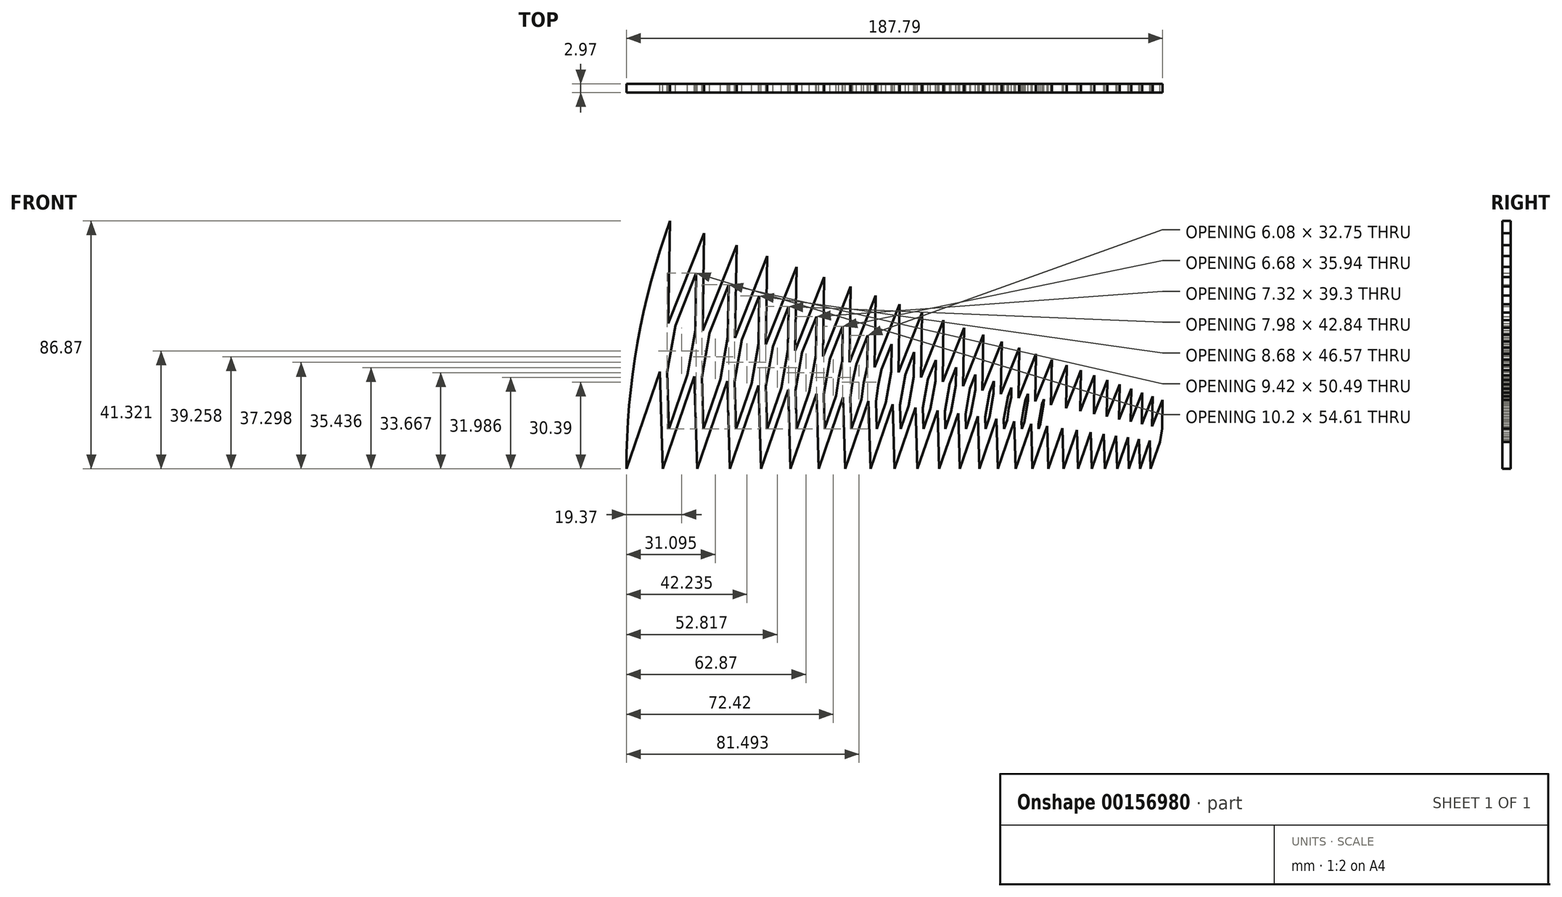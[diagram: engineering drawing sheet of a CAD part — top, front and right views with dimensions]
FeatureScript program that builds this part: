
annotation { "Feature Type Name" : "Feature", "Feature Type Description" : "" }
export const myFeature = defineFeature(function(context is Context, id is Id, definition is map)
    precondition{}
    {
        {
            var Q0;
            Q0=qCreatedBy(makeId("Front.planeOp"),FACE);
            var sketch = newSketch(context, id + "F0", { "sketchPlane" : qUnion([Q0])});
            skLineSegment(sketch, "E0", {"start": v(-94.98, 0) * mm, "end": v(159.02, 0) * mm, "construction": true});
            skLineSegment(sketch, "E1", {"start": v(159.02, 0) * mm, "end": v(-91.12, 44.1) * mm, "construction": true});
            skLineSegment(sketch, "E2", {"start": v(159.02, 0) * mm, "end": v(-92.51, 35.35) * mm, "construction": true});
            skLineSegment(sketch, "E3", {"start": v(91.81, 9.44) * mm, "end": v(88.56, 0) * mm});
            skLineSegment(sketch, "E4", {"start": v(88.56, 0) * mm, "end": v(88.28, 9.94) * mm});
            skLineSegment(sketch, "E5", {"start": v(88.28, 9.94) * mm, "end": v(84.85, 0) * mm});
            skLineSegment(sketch, "E6", {"start": v(84.85, 0) * mm, "end": v(84.55, 10.47) * mm});
            skLineSegment(sketch, "E7", {"start": v(84.55, 10.47) * mm, "end": v(80.95, 0) * mm});
            skLineSegment(sketch, "E8", {"start": v(80.95, 0) * mm, "end": v(80.63, 11.02) * mm});
            skLineSegment(sketch, "E9", {"start": v(80.63, 11.02) * mm, "end": v(76.84, 0) * mm});
            skLineSegment(sketch, "E10", {"start": v(76.84, 0) * mm, "end": v(76.5, 11.6) * mm});
            skLineSegment(sketch, "E11", {"start": v(76.5, 11.6) * mm, "end": v(72.51, 0) * mm});
            skLineSegment(sketch, "E12", {"start": v(72.51, 0) * mm, "end": v(72.17, 12.2) * mm});
            skLineSegment(sketch, "E13", {"start": v(72.17, 12.2) * mm, "end": v(67.96, 0) * mm});
            skLineSegment(sketch, "E14", {"start": v(67.96, 0) * mm, "end": v(67.6, 12.85) * mm});
            skLineSegment(sketch, "E15", {"start": v(67.6, 12.85) * mm, "end": v(63.17, 0) * mm});
            skLineSegment(sketch, "E16", {"start": v(63.17, 0) * mm, "end": v(62.78, 13.52) * mm});
            skLineSegment(sketch, "E17", {"start": v(62.78, 13.52) * mm, "end": v(58.12, 0) * mm});
            skLineSegment(sketch, "E18", {"start": v(58.12, 0) * mm, "end": v(57.72, 14.24) * mm});
            skLineSegment(sketch, "E19", {"start": v(57.72, 14.24) * mm, "end": v(52.81, 0) * mm});
            skLineSegment(sketch, "E20", {"start": v(52.81, 0) * mm, "end": v(52.39, 14.99) * mm});
            skLineSegment(sketch, "E21", {"start": v(52.39, 14.99) * mm, "end": v(47.22, 0) * mm});
            skLineSegment(sketch, "E22", {"start": v(47.22, 0) * mm, "end": v(46.77, 15.77) * mm});
            skLineSegment(sketch, "E23", {"start": v(46.77, 15.77) * mm, "end": v(41.34, 0) * mm});
            skLineSegment(sketch, "E24", {"start": v(41.34, 0) * mm, "end": v(40.87, 16.6) * mm});
            skLineSegment(sketch, "E25", {"start": v(40.87, 16.6) * mm, "end": v(35.15, 0) * mm});
            skLineSegment(sketch, "E26", {"start": v(35.15, 0) * mm, "end": v(34.65, 17.48) * mm});
            skLineSegment(sketch, "E27", {"start": v(34.65, 17.48) * mm, "end": v(28.63, 0) * mm});
            skLineSegment(sketch, "E28", {"start": v(28.63, 0) * mm, "end": v(28.1, 18.4) * mm});
            skLineSegment(sketch, "E29", {"start": v(28.1, 18.4) * mm, "end": v(21.77, 0) * mm});
            skLineSegment(sketch, "E30", {"start": v(21.77, 0) * mm, "end": v(21.21, 19.37) * mm});
            skLineSegment(sketch, "E31", {"start": v(21.21, 19.37) * mm, "end": v(14.54, 0) * mm});
            skLineSegment(sketch, "E32", {"start": v(14.54, 0) * mm, "end": v(13.96, 20.39) * mm});
            skLineSegment(sketch, "E33", {"start": v(13.96, 20.39) * mm, "end": v(6.94, 0) * mm});
            skLineSegment(sketch, "E34", {"start": v(6.94, 0) * mm, "end": v(6.33, 21.46) * mm});
            skLineSegment(sketch, "E35", {"start": v(6.33, 21.46) * mm, "end": v(-1.07, 0) * mm});
            skLineSegment(sketch, "E36", {"start": v(-1.07, 0) * mm, "end": v(-1.71, 22.59) * mm});
            skLineSegment(sketch, "E37", {"start": v(-1.71, 22.59) * mm, "end": v(-9.5, 0) * mm});
            skLineSegment(sketch, "E38", {"start": v(-18.36, 0) * mm, "end": v(-19.07, 25.03) * mm});
            skLineSegment(sketch, "E39", {"start": v(-19.07, 25.03) * mm, "end": v(-27.7, 0) * mm});
            skLineSegment(sketch, "E40", {"start": v(-27.7, 0) * mm, "end": v(-28.45, 26.35) * mm});
            skLineSegment(sketch, "E41", {"start": v(-28.45, 26.35) * mm, "end": v(-37.52, 0) * mm});
            skLineSegment(sketch, "E42", {"start": v(-37.52, 0) * mm, "end": v(-38.31, 27.73) * mm});
            skLineSegment(sketch, "E43", {"start": v(-38.31, 27.73) * mm, "end": v(-47.87, 0) * mm});
            skLineSegment(sketch, "E44", {"start": v(-47.87, 0) * mm, "end": v(-48.7, 29.2) * mm});
            skLineSegment(sketch, "E45", {"start": v(-48.7, 29.2) * mm, "end": v(-58.76, 0) * mm});
            skLineSegment(sketch, "E46", {"start": v(-18.36, 0) * mm, "end": v(-10.17, 23.78) * mm});
            skLineSegment(sketch, "E47", {"start": v(-10.17, 23.78) * mm, "end": v(-9.5, 0) * mm});
            skLineSegment(sketch, "E48", {"start": v(-58.76, 0) * mm, "end": v(-59.63, 30.73) * mm});
            skLineSegment(sketch, "E49", {"start": v(-59.63, 30.73) * mm, "end": v(-70.22, 0) * mm});
            skLineSegment(sketch, "E50", {"start": v(-70.22, 0) * mm, "end": v(-71.14, 32.35) * mm});
            skLineSegment(sketch, "E51", {"start": v(-71.14, 32.35) * mm, "end": v(-82.28, 0) * mm});
            skLineSegment(sketch, "E52", {"start": v(-82.28, 0) * mm, "end": v(-83.25, 34.05) * mm});
            skLineSegment(sketch, "E53", {"start": v(-83.25, 34.05) * mm, "end": v(-94.98, 0) * mm});
            skLineSegment(sketch, "E54.MirrorCS", {"start": v(-80.29, 50.87) * mm, "end": v(-79.67, 86.87) * mm});
            skLineSegment(sketch, "E55.MirrorCS", {"start": v(-67.73, 82.53) * mm, "end": v(-80.29, 50.87) * mm});
            skLineSegment(sketch, "E56.MirrorCS", {"start": v(-56.4, 78.4) * mm, "end": v(-68.32, 48.32) * mm});
            skLineSegment(sketch, "E57.MirrorCS", {"start": v(-56.96, 45.9) * mm, "end": v(-56.4, 78.4) * mm});
            skLineSegment(sketch, "E58.MirrorCS", {"start": v(-45.62, 74.48) * mm, "end": v(-56.96, 45.9) * mm});
            skLineSegment(sketch, "E59.MirrorCS", {"start": v(-46.16, 43.61) * mm, "end": v(-45.62, 74.48) * mm});
            skLineSegment(sketch, "E60.MirrorCS", {"start": v(-35.4, 70.76) * mm, "end": v(-46.16, 43.61) * mm});
            skLineSegment(sketch, "E61.MirrorCS", {"start": v(-35.9, 41.43) * mm, "end": v(-35.4, 70.76) * mm});
            skLineSegment(sketch, "E62.MirrorCS", {"start": v(-25.67, 67.22) * mm, "end": v(-35.9, 41.43) * mm});
            skLineSegment(sketch, "E63.MirrorCS", {"start": v(-26.15, 39.36) * mm, "end": v(-25.67, 67.22) * mm});
            skLineSegment(sketch, "E64.MirrorCS", {"start": v(-16.44, 63.86) * mm, "end": v(-26.15, 39.36) * mm});
            skLineSegment(sketch, "E65.MirrorCS", {"start": v(-16.9, 37.4) * mm, "end": v(-16.44, 63.86) * mm});
            skLineSegment(sketch, "E66.MirrorCS", {"start": v(-7.66, 60.67) * mm, "end": v(-16.9, 37.4) * mm});
            skLineSegment(sketch, "E67.MirrorCS", {"start": v(-7.66, 60.67) * mm, "end": v(-8.1, 35.52) * mm});
            skLineSegment(sketch, "E68.MirrorCS", {"start": v(-8.1, 35.52) * mm, "end": v(0.67, 57.63) * mm});
            skLineSegment(sketch, "E69.MirrorCS", {"start": v(0.26, 33.75) * mm, "end": v(0.67, 57.63) * mm});
            skLineSegment(sketch, "E70.MirrorCS", {"start": v(8.59, 54.75) * mm, "end": v(0.26, 33.75) * mm});
            skLineSegment(sketch, "E71.MirrorCS", {"start": v(8.2, 32.06) * mm, "end": v(8.59, 54.75) * mm});
            skLineSegment(sketch, "E72.MirrorCS", {"start": v(16.1, 52.01) * mm, "end": v(8.2, 32.06) * mm});
            skLineSegment(sketch, "E73.MirrorCS", {"start": v(23.25, 49.41) * mm, "end": v(15.74, 30.46) * mm});
            skLineSegment(sketch, "E74.MirrorCS", {"start": v(22.9, 28.93) * mm, "end": v(23.25, 49.41) * mm});
            skLineSegment(sketch, "E75.MirrorCS", {"start": v(30.04, 46.94) * mm, "end": v(22.9, 28.93) * mm});
            skLineSegment(sketch, "E76.MirrorCS", {"start": v(15.74, 30.46) * mm, "end": v(16.1, 52.01) * mm});
            skLineSegment(sketch, "E77.MirrorCS", {"start": v(29.7, 27.49) * mm, "end": v(30.04, 46.94) * mm});
            skLineSegment(sketch, "E78.MirrorCS", {"start": v(36.5, 44.6) * mm, "end": v(29.7, 27.49) * mm});
            skLineSegment(sketch, "E79.MirrorCS", {"start": v(36.17, 26.11) * mm, "end": v(36.5, 44.6) * mm});
            skLineSegment(sketch, "E80.MirrorCS", {"start": v(42.62, 42.37) * mm, "end": v(36.17, 26.11) * mm});
            skLineSegment(sketch, "E81.MirrorCS", {"start": v(42.31, 24.8) * mm, "end": v(42.62, 42.37) * mm});
            skLineSegment(sketch, "E82.MirrorCS", {"start": v(48.44, 40.25) * mm, "end": v(42.31, 24.8) * mm});
            skLineSegment(sketch, "E83.MirrorCS", {"start": v(48.15, 23.57) * mm, "end": v(48.44, 40.25) * mm});
            skLineSegment(sketch, "E84.MirrorCS", {"start": v(53.97, 38.24) * mm, "end": v(48.15, 23.57) * mm});
            skLineSegment(sketch, "E85.MirrorCS", {"start": v(53.7, 22.39) * mm, "end": v(53.97, 38.24) * mm});
            skLineSegment(sketch, "E86.MirrorCS", {"start": v(59.22, 36.32) * mm, "end": v(53.7, 22.39) * mm});
            skLineSegment(sketch, "E87.MirrorCS", {"start": v(58.96, 21.27) * mm, "end": v(59.22, 36.32) * mm});
            skLineSegment(sketch, "E88.MirrorCS", {"start": v(64.2, 34.5) * mm, "end": v(58.96, 21.27) * mm});
            skLineSegment(sketch, "E89.MirrorCS", {"start": v(63.96, 20.2) * mm, "end": v(64.2, 34.5) * mm});
            skLineSegment(sketch, "E90.MirrorCS", {"start": v(68.95, 32.78) * mm, "end": v(63.96, 20.2) * mm});
            skLineSegment(sketch, "E91.MirrorCS", {"start": v(68.71, 19.2) * mm, "end": v(68.95, 32.78) * mm});
            skLineSegment(sketch, "E92.MirrorCS", {"start": v(73.45, 31.14) * mm, "end": v(68.71, 19.2) * mm});
            skLineSegment(sketch, "E93.MirrorCS", {"start": v(73.23, 18.23) * mm, "end": v(73.45, 31.14) * mm});
            skLineSegment(sketch, "E94.MirrorCS", {"start": v(77.73, 29.59) * mm, "end": v(73.23, 18.23) * mm});
            skLineSegment(sketch, "E95.MirrorCS", {"start": v(77.52, 17.32) * mm, "end": v(77.73, 29.59) * mm});
            skLineSegment(sketch, "E96.MirrorCS", {"start": v(81.8, 28.1) * mm, "end": v(77.52, 17.32) * mm});
            skLineSegment(sketch, "E97.MirrorCS", {"start": v(81.6, 16.46) * mm, "end": v(81.8, 28.1) * mm});
            skLineSegment(sketch, "E98.MirrorCS", {"start": v(85.66, 26.7) * mm, "end": v(81.6, 16.46) * mm});
            skLineSegment(sketch, "E99.MirrorCS", {"start": v(85.46, 15.63) * mm, "end": v(85.66, 26.7) * mm});
            skLineSegment(sketch, "E100.MirrorCS", {"start": v(89.32, 25.37) * mm, "end": v(85.46, 15.63) * mm});
            skLineSegment(sketch, "E101.MirrorCS", {"start": v(89.14, 14.85) * mm, "end": v(89.32, 25.37) * mm});
            skLineSegment(sketch, "E102.MirrorCS", {"start": v(92.8, 24.1) * mm, "end": v(89.14, 14.85) * mm});
            skLineSegment(sketch, "E103.MirrorCS", {"start": v(92.64, 14.1) * mm, "end": v(92.8, 24.1) * mm});
            skLineSegment(sketch, "E104.MirrorCS", {"start": v(-68.32, 48.32) * mm, "end": v(-67.73, 82.53) * mm});
            skLineSegment(sketch, "E105", {"start": v(159.02, 0) * mm, "end": v(-79.67, 86.87) * mm, "construction": true});
            skArc(sketch, "E106", {"start": v(-79.67, 86.87) * mm, "mid": v(-91.12, 44.1) * mm, "end": v(-94.98, 0) * mm});
            skLineSegment(sketch, "E107", {"start": v(-83.25, 34.05) * mm, "end": v(-81.77, 42.46) * mm});
            skLineSegment(sketch, "E108", {"start": v(-71.14, 32.35) * mm, "end": v(-69.73, 40.33) * mm});
            skLineSegment(sketch, "E109", {"start": v(-59.63, 30.73) * mm, "end": v(-58.3, 38.32) * mm});
            skLineSegment(sketch, "E110", {"start": v(-48.7, 29.2) * mm, "end": v(-47.43, 36.4) * mm});
            skLineSegment(sketch, "E111", {"start": v(-38.31, 27.73) * mm, "end": v(-37.1, 34.58) * mm});
            skLineSegment(sketch, "E112.MirrorCS", {"start": v(-80.29, 50.87) * mm, "end": v(-81.77, 42.46) * mm});
            skLineSegment(sketch, "E113.MirrorCS", {"start": v(-68.32, 48.32) * mm, "end": v(-69.73, 40.33) * mm});
            skLineSegment(sketch, "E114.MirrorCS", {"start": v(-56.96, 45.9) * mm, "end": v(-58.3, 38.32) * mm});
            skLineSegment(sketch, "E115.MirrorCS", {"start": v(-46.16, 43.61) * mm, "end": v(-47.43, 36.4) * mm});
            skLineSegment(sketch, "E116.MirrorCS", {"start": v(-35.9, 41.43) * mm, "end": v(-37.1, 34.58) * mm});
            skLineSegment(sketch, "E117.0", {"start": v(-70.86, 48.57) * mm, "end": v(-70.51, 68.63) * mm});
            skLineSegment(sketch, "E117.1", {"start": v(-70.86, 48.57) * mm, "end": v(-72.23, 40.78) * mm});
            skLineSegment(sketch, "E117.2", {"start": v(-70.51, 68.63) * mm, "end": v(-77.83, 50.17) * mm});
            skLineSegment(sketch, "E117.3", {"start": v(-73.6, 32.98) * mm, "end": v(-72.23, 40.78) * mm});
            skLineSegment(sketch, "E117.4", {"start": v(-77.83, 50.17) * mm, "end": v(-79.27, 42.02) * mm});
            skLineSegment(sketch, "E117.5", {"start": v(-80.7, 33.86) * mm, "end": v(-79.27, 42.02) * mm});
            skLineSegment(sketch, "E117.6", {"start": v(-80.14, 14.02) * mm, "end": v(-80.7, 33.86) * mm});
            skLineSegment(sketch, "E117.7", {"start": v(-73.6, 32.98) * mm, "end": v(-80.14, 14.02) * mm});
            skLineSegment(sketch, "E118", {"start": v(-28.45, 26.35) * mm, "end": v(-27.3, 32.85) * mm});
            skLineSegment(sketch, "E119", {"start": v(-19.07, 25.03) * mm, "end": v(-18.2, 31.25) * mm});
            skLineSegment(sketch, "E120", {"start": v(-10.17, 23.78) * mm, "end": v(-9.34, 29.69) * mm});
            skLineSegment(sketch, "E121", {"start": v(92.64, 14.1) * mm, "end": v(91.81, 9.44) * mm});
            skLineSegment(sketch, "E122.0", {"start": v(-59.18, 64.5) * mm, "end": v(-65.87, 47.63) * mm});
            skLineSegment(sketch, "E122.1", {"start": v(-59.5, 46.15) * mm, "end": v(-59.18, 64.5) * mm});
            skLineSegment(sketch, "E122.2", {"start": v(-65.87, 47.63) * mm, "end": v(-67.23, 39.9) * mm});
            skLineSegment(sketch, "E122.3", {"start": v(-59.5, 46.15) * mm, "end": v(-60.8, 38.76) * mm});
            skLineSegment(sketch, "E122.4", {"start": v(-68.6, 32.16) * mm, "end": v(-67.23, 39.9) * mm});
            skLineSegment(sketch, "E122.5", {"start": v(-68.08, 14.02) * mm, "end": v(-68.6, 32.16) * mm});
            skLineSegment(sketch, "E122.6", {"start": v(-62.1, 31.37) * mm, "end": v(-68.08, 14.02) * mm});
            skLineSegment(sketch, "E122.7", {"start": v(-62.1, 31.37) * mm, "end": v(-60.8, 38.76) * mm});
            skLineSegment(sketch, "E123.MirrorCS", {"start": v(-26.15, 39.36) * mm, "end": v(-27.3, 32.85) * mm});
            skLineSegment(sketch, "E124.MirrorCS", {"start": v(-16.9, 37.4) * mm, "end": v(-18.2, 31.25) * mm});
            skLineSegment(sketch, "E125.MirrorCS", {"start": v(-8.1, 35.52) * mm, "end": v(-9.34, 29.69) * mm});
            skLineSegment(sketch, "E126.0", {"start": v(-48.4, 60.58) * mm, "end": v(-54.5, 45.21) * mm});
            skLineSegment(sketch, "E126.1", {"start": v(-48.7, 43.86) * mm, "end": v(-48.4, 60.58) * mm});
            skLineSegment(sketch, "E126.2", {"start": v(-54.5, 45.21) * mm, "end": v(-55.8, 37.88) * mm});
            skLineSegment(sketch, "E126.3", {"start": v(-48.7, 43.86) * mm, "end": v(-49.93, 36.84) * mm});
            skLineSegment(sketch, "E126.4", {"start": v(-57.09, 30.54) * mm, "end": v(-55.8, 37.88) * mm});
            skLineSegment(sketch, "E126.5", {"start": v(-56.62, 14.02) * mm, "end": v(-57.09, 30.54) * mm});
            skLineSegment(sketch, "E126.6", {"start": v(-51.17, 29.83) * mm, "end": v(-56.62, 14.02) * mm});
            skLineSegment(sketch, "E126.7", {"start": v(-51.17, 29.83) * mm, "end": v(-49.93, 36.84) * mm});
            skLineSegment(sketch, "E127.0", {"start": v(-38.17, 56.86) * mm, "end": v(-43.7, 42.92) * mm});
            skLineSegment(sketch, "E127.1", {"start": v(-38.44, 41.67) * mm, "end": v(-38.17, 56.86) * mm});
            skLineSegment(sketch, "E127.2", {"start": v(-43.7, 42.92) * mm, "end": v(-44.93, 35.96) * mm});
            skLineSegment(sketch, "E127.3", {"start": v(-38.44, 41.67) * mm, "end": v(-39.6, 35.02) * mm});
            skLineSegment(sketch, "E127.4", {"start": v(-46.15, 29) * mm, "end": v(-44.93, 35.96) * mm});
            skLineSegment(sketch, "E127.5", {"start": v(-45.73, 14.02) * mm, "end": v(-46.15, 29) * mm});
            skLineSegment(sketch, "E127.6", {"start": v(-40.78, 28.37) * mm, "end": v(-45.73, 14.02) * mm});
            skLineSegment(sketch, "E127.7", {"start": v(-40.78, 28.37) * mm, "end": v(-39.6, 35.02) * mm});
            skLineSegment(sketch, "E128.0", {"start": v(-28.45, 53.32) * mm, "end": v(-33.44, 40.73) * mm});
            skLineSegment(sketch, "E128.1", {"start": v(-28.69, 39.6) * mm, "end": v(-28.45, 53.32) * mm});
            skLineSegment(sketch, "E128.2", {"start": v(-33.44, 40.73) * mm, "end": v(-34.6, 34.14) * mm});
            skLineSegment(sketch, "E128.3", {"start": v(-28.69, 39.6) * mm, "end": v(-29.8, 33.3) * mm});
            skLineSegment(sketch, "E128.4", {"start": v(-35.77, 27.55) * mm, "end": v(-34.6, 34.14) * mm});
            skLineSegment(sketch, "E128.5", {"start": v(-35.38, 14.02) * mm, "end": v(-35.77, 27.55) * mm});
            skLineSegment(sketch, "E128.6", {"start": v(-30.91, 26.98) * mm, "end": v(-35.38, 14.02) * mm});
            skLineSegment(sketch, "E128.7", {"start": v(-30.91, 26.98) * mm, "end": v(-29.8, 33.3) * mm});
            skLineSegment(sketch, "E129.0", {"start": v(-19.22, 49.96) * mm, "end": v(-23.7, 38.66) * mm});
            skLineSegment(sketch, "E129.1", {"start": v(-19.43, 37.68) * mm, "end": v(-19.22, 49.96) * mm});
            skLineSegment(sketch, "E129.2", {"start": v(-23.7, 38.66) * mm, "end": v(-24.8, 32.41) * mm});
            skLineSegment(sketch, "E129.3", {"start": v(-19.43, 37.68) * mm, "end": v(-20.7, 31.69) * mm});
            skLineSegment(sketch, "E129.4", {"start": v(-25.9, 26.16) * mm, "end": v(-24.8, 32.41) * mm});
            skLineSegment(sketch, "E129.5", {"start": v(-25.56, 14.02) * mm, "end": v(-25.9, 26.16) * mm});
            skLineSegment(sketch, "E129.6", {"start": v(-21.56, 25.62) * mm, "end": v(-25.56, 14.02) * mm});
            skLineSegment(sketch, "E129.7", {"start": v(-21.56, 25.62) * mm, "end": v(-20.7, 31.69) * mm});
            skLineSegment(sketch, "E130.0", {"start": v(-10.45, 46.76) * mm, "end": v(-14.45, 36.65) * mm});
            skLineSegment(sketch, "E130.1", {"start": v(-10.45, 46.76) * mm, "end": v(-10.63, 35.81) * mm});
            skLineSegment(sketch, "E130.2", {"start": v(-14.45, 36.65) * mm, "end": v(-15.7, 30.8) * mm});
            skLineSegment(sketch, "E130.3", {"start": v(-10.63, 35.81) * mm, "end": v(-11.84, 30.13) * mm});
            skLineSegment(sketch, "E130.4", {"start": v(-16.53, 24.89) * mm, "end": v(-15.7, 30.8) * mm});
            skLineSegment(sketch, "E130.5", {"start": v(-16.22, 14.02) * mm, "end": v(-16.53, 24.89) * mm});
            skLineSegment(sketch, "E130.6", {"start": v(-16.22, 14.02) * mm, "end": v(-12.65, 24.37) * mm});
            skLineSegment(sketch, "E130.7", {"start": v(-12.65, 24.37) * mm, "end": v(-11.84, 30.13) * mm});
            skLineSegment(sketch, "E131", {"start": v(-1.71, 22.59) * mm, "end": v(-0.73, 28.17) * mm});
            skLineSegment(sketch, "E132", {"start": v(6.33, 21.46) * mm, "end": v(7.26, 26.76) * mm});
            skLineSegment(sketch, "E133", {"start": v(13.96, 20.39) * mm, "end": v(14.85, 25.42) * mm});
            skLineSegment(sketch, "E134", {"start": v(21.21, 19.37) * mm, "end": v(22.06, 24.15) * mm});
            skLineSegment(sketch, "E135.MirrorCS", {"start": v(0.26, 33.75) * mm, "end": v(-0.73, 28.17) * mm});
            skLineSegment(sketch, "E136.MirrorCS", {"start": v(8.2, 32.06) * mm, "end": v(7.26, 26.76) * mm});
            skLineSegment(sketch, "E137.MirrorCS", {"start": v(15.74, 30.46) * mm, "end": v(14.85, 25.42) * mm});
            skLineSegment(sketch, "E138.MirrorCS", {"start": v(22.9, 28.93) * mm, "end": v(22.06, 24.15) * mm});
            skLineSegment(sketch, "E139.0", {"start": v(-5.66, 34.78) * mm, "end": v(-2.11, 43.73) * mm});
            skLineSegment(sketch, "E139.1", {"start": v(-2.28, 33.99) * mm, "end": v(-2.11, 43.73) * mm});
            skLineSegment(sketch, "E139.2", {"start": v(-5.66, 34.78) * mm, "end": v(-6.84, 29.24) * mm});
            skLineSegment(sketch, "E139.3", {"start": v(-2.28, 33.99) * mm, "end": v(-3.23, 28.6) * mm});
            skLineSegment(sketch, "E139.4", {"start": v(-7.63, 23.64) * mm, "end": v(-6.84, 29.24) * mm});
            skLineSegment(sketch, "E139.5", {"start": v(-7.63, 23.64) * mm, "end": v(-7.35, 14.02) * mm});
            skLineSegment(sketch, "E139.6", {"start": v(-4.18, 23.23) * mm, "end": v(-7.35, 14.02) * mm});
            skLineSegment(sketch, "E139.7", {"start": v(-4.18, 23.23) * mm, "end": v(-3.23, 28.6) * mm});
            skLineSegment(sketch, "E140.0", {"start": v(5.8, 40.85) * mm, "end": v(2.71, 33.05) * mm});
            skLineSegment(sketch, "E140.1", {"start": v(5.66, 32.3) * mm, "end": v(5.8, 40.85) * mm});
            skLineSegment(sketch, "E140.2", {"start": v(2.71, 33.05) * mm, "end": v(1.77, 27.73) * mm});
            skLineSegment(sketch, "E140.3", {"start": v(5.66, 32.3) * mm, "end": v(4.76, 27.2) * mm});
            skLineSegment(sketch, "E140.4", {"start": v(0.84, 22.4) * mm, "end": v(1.77, 27.73) * mm});
            skLineSegment(sketch, "E140.5", {"start": v(1.07, 14.02) * mm, "end": v(0.84, 22.4) * mm});
            skLineSegment(sketch, "E140.6", {"start": v(3.86, 22.1) * mm, "end": v(1.07, 14.02) * mm});
            skLineSegment(sketch, "E140.7", {"start": v(3.86, 22.1) * mm, "end": v(4.76, 27.2) * mm});
            skLineSegment(sketch, "E141.0", {"start": v(13.33, 38.11) * mm, "end": v(10.65, 31.36) * mm});
            skLineSegment(sketch, "E141.1", {"start": v(13.2, 30.7) * mm, "end": v(13.33, 38.11) * mm});
            skLineSegment(sketch, "E141.2", {"start": v(10.65, 31.36) * mm, "end": v(9.76, 26.32) * mm});
            skLineSegment(sketch, "E141.3", {"start": v(13.2, 30.7) * mm, "end": v(12.35, 25.86) * mm});
            skLineSegment(sketch, "E141.4", {"start": v(8.87, 21.27) * mm, "end": v(9.76, 26.32) * mm});
            skLineSegment(sketch, "E141.5", {"start": v(9.08, 14.02) * mm, "end": v(8.87, 21.27) * mm});
            skLineSegment(sketch, "E141.6", {"start": v(11.5, 21.02) * mm, "end": v(9.08, 14.02) * mm});
            skLineSegment(sketch, "E141.7", {"start": v(11.5, 21.02) * mm, "end": v(12.35, 25.86) * mm});
            skLineSegment(sketch, "E142.0", {"start": v(20.47, 35.51) * mm, "end": v(18.2, 29.76) * mm});
            skLineSegment(sketch, "E142.1", {"start": v(20.36, 29.18) * mm, "end": v(20.47, 35.51) * mm});
            skLineSegment(sketch, "E142.2", {"start": v(18.2, 29.76) * mm, "end": v(17.35, 24.98) * mm});
            skLineSegment(sketch, "E142.3", {"start": v(20.36, 29.18) * mm, "end": v(19.55, 24.6) * mm});
            skLineSegment(sketch, "E142.4", {"start": v(16.5, 20.2) * mm, "end": v(17.35, 24.98) * mm});
            skLineSegment(sketch, "E142.5", {"start": v(16.68, 14.02) * mm, "end": v(16.5, 20.2) * mm});
            skLineSegment(sketch, "E142.6", {"start": v(18.75, 20) * mm, "end": v(16.68, 14.02) * mm});
            skLineSegment(sketch, "E142.7", {"start": v(18.75, 20) * mm, "end": v(19.55, 24.6) * mm});
            skLineSegment(sketch, "E143", {"start": v(28.1, 18.4) * mm, "end": v(28.9, 22.94) * mm});
            skLineSegment(sketch, "E144", {"start": v(34.65, 17.48) * mm, "end": v(35.4, 21.8) * mm});
            skLineSegment(sketch, "E145", {"start": v(40.87, 16.6) * mm, "end": v(41.45, 20.73) * mm});
            skLineSegment(sketch, "E146.MirrorCS", {"start": v(29.7, 27.49) * mm, "end": v(28.9, 22.94) * mm});
            skLineSegment(sketch, "E147.MirrorCS", {"start": v(36.17, 26.11) * mm, "end": v(35.4, 21.8) * mm});
            skLineSegment(sketch, "E148.MirrorCS", {"start": v(42.31, 24.8) * mm, "end": v(41.45, 20.73) * mm});
            skLineSegment(sketch, "E149.0", {"start": v(27.26, 33.04) * mm, "end": v(25.36, 28.24) * mm});
            skLineSegment(sketch, "E149.1", {"start": v(27.17, 27.73) * mm, "end": v(27.26, 33.04) * mm});
            skLineSegment(sketch, "E149.2", {"start": v(25.36, 28.24) * mm, "end": v(24.56, 23.7) * mm});
            skLineSegment(sketch, "E149.3", {"start": v(27.17, 27.73) * mm, "end": v(26.4, 23.38) * mm});
            skLineSegment(sketch, "E149.4", {"start": v(23.76, 19.18) * mm, "end": v(24.56, 23.7) * mm});
            skLineSegment(sketch, "E149.5", {"start": v(23.9, 14.02) * mm, "end": v(23.76, 19.18) * mm});
            skLineSegment(sketch, "E149.6", {"start": v(25.64, 19.04) * mm, "end": v(23.9, 14.02) * mm});
            skLineSegment(sketch, "E149.7", {"start": v(25.64, 19.04) * mm, "end": v(26.4, 23.38) * mm});
            skLineSegment(sketch, "E150.0", {"start": v(33.7, 30.7) * mm, "end": v(32.16, 26.8) * mm});
            skLineSegment(sketch, "E150.1", {"start": v(33.63, 26.36) * mm, "end": v(33.7, 30.7) * mm});
            skLineSegment(sketch, "E150.2", {"start": v(32.16, 26.8) * mm, "end": v(31.4, 22.5) * mm});
            skLineSegment(sketch, "E150.3", {"start": v(33.63, 26.36) * mm, "end": v(32.9, 22.24) * mm});
            skLineSegment(sketch, "E150.4", {"start": v(30.65, 18.21) * mm, "end": v(31.4, 22.5) * mm});
            skLineSegment(sketch, "E150.5", {"start": v(30.77, 14.02) * mm, "end": v(30.65, 18.21) * mm});
            skLineSegment(sketch, "E150.6", {"start": v(32.18, 18.12) * mm, "end": v(30.77, 14.02) * mm});
            skLineSegment(sketch, "E150.7", {"start": v(32.18, 18.12) * mm, "end": v(32.9, 22.24) * mm});
            skLineSegment(sketch, "E151.0", {"start": v(39.84, 28.46) * mm, "end": v(38.63, 25.42) * mm});
            skLineSegment(sketch, "E151.1", {"start": v(39.78, 25.1) * mm, "end": v(39.84, 28.46) * mm});
            skLineSegment(sketch, "E151.2", {"start": v(38.63, 25.42) * mm, "end": v(37.91, 21.35) * mm});
            skLineSegment(sketch, "E151.3", {"start": v(39.78, 25.1) * mm, "end": v(38.94, 21.17) * mm});
            skLineSegment(sketch, "E151.4", {"start": v(37.2, 17.3) * mm, "end": v(37.91, 21.35) * mm});
            skLineSegment(sketch, "E151.5", {"start": v(37.29, 14.02) * mm, "end": v(37.2, 17.3) * mm});
            skLineSegment(sketch, "E151.6", {"start": v(38.39, 17.2) * mm, "end": v(37.29, 14.02) * mm});
            skLineSegment(sketch, "E151.7", {"start": v(38.39, 17.2) * mm, "end": v(38.94, 21.17) * mm});
            skLineSegment(sketch, "E152", {"start": v(46.77, 15.77) * mm, "end": v(47.46, 19.67) * mm});
            skLineSegment(sketch, "E153.MirrorCS", {"start": v(48.15, 23.57) * mm, "end": v(47.46, 19.67) * mm});
            skLineSegment(sketch, "E154.0", {"start": v(45.66, 26.35) * mm, "end": v(44.75, 24.07) * mm});
            skLineSegment(sketch, "E154.1", {"start": v(45.61, 23.8) * mm, "end": v(45.66, 26.35) * mm});
            skLineSegment(sketch, "E154.2", {"start": v(44.75, 24.07) * mm, "end": v(43.95, 20.29) * mm});
            skLineSegment(sketch, "E154.3", {"start": v(45.61, 23.8) * mm, "end": v(44.96, 20.11) * mm});
            skLineSegment(sketch, "E154.4", {"start": v(43.41, 16.46) * mm, "end": v(43.95, 20.29) * mm});
            skLineSegment(sketch, "E154.5", {"start": v(43.48, 14.02) * mm, "end": v(43.41, 16.46) * mm});
            skLineSegment(sketch, "E154.6", {"start": v(44.3, 16.41) * mm, "end": v(43.48, 14.02) * mm});
            skLineSegment(sketch, "E154.7", {"start": v(44.3, 16.41) * mm, "end": v(44.96, 20.11) * mm});
            skLineSegment(sketch, "E155", {"start": v(52.39, 14.99) * mm, "end": v(53.04, 18.69) * mm});
            skLineSegment(sketch, "E156.MirrorCS", {"start": v(53.7, 22.39) * mm, "end": v(53.04, 18.69) * mm});
            skLineSegment(sketch, "E157.0", {"start": v(51.19, 24.33) * mm, "end": v(50.6, 22.87) * mm});
            skLineSegment(sketch, "E157.1", {"start": v(51.16, 22.63) * mm, "end": v(51.19, 24.33) * mm});
            skLineSegment(sketch, "E157.2", {"start": v(50.6, 22.87) * mm, "end": v(49.96, 19.23) * mm});
            skLineSegment(sketch, "E157.3", {"start": v(51.16, 22.63) * mm, "end": v(50.54, 19.13) * mm});
            skLineSegment(sketch, "E157.4", {"start": v(49.32, 15.59) * mm, "end": v(49.96, 19.23) * mm});
            skLineSegment(sketch, "E157.5", {"start": v(49.37, 14.02) * mm, "end": v(49.32, 15.59) * mm});
            skLineSegment(sketch, "E157.6", {"start": v(49.92, 15.62) * mm, "end": v(49.37, 14.02) * mm});
            skLineSegment(sketch, "E157.7", {"start": v(49.92, 15.62) * mm, "end": v(50.54, 19.13) * mm});
            skSolve(sketch);
        }
        {
            var Q0;
            Q0 = qSketchRegion(id + "F0", true);
            extrude(context, id + "F1", {"entities" : qUnion([Q0]), "depth" : 2.97 * mm});
        }
    });
